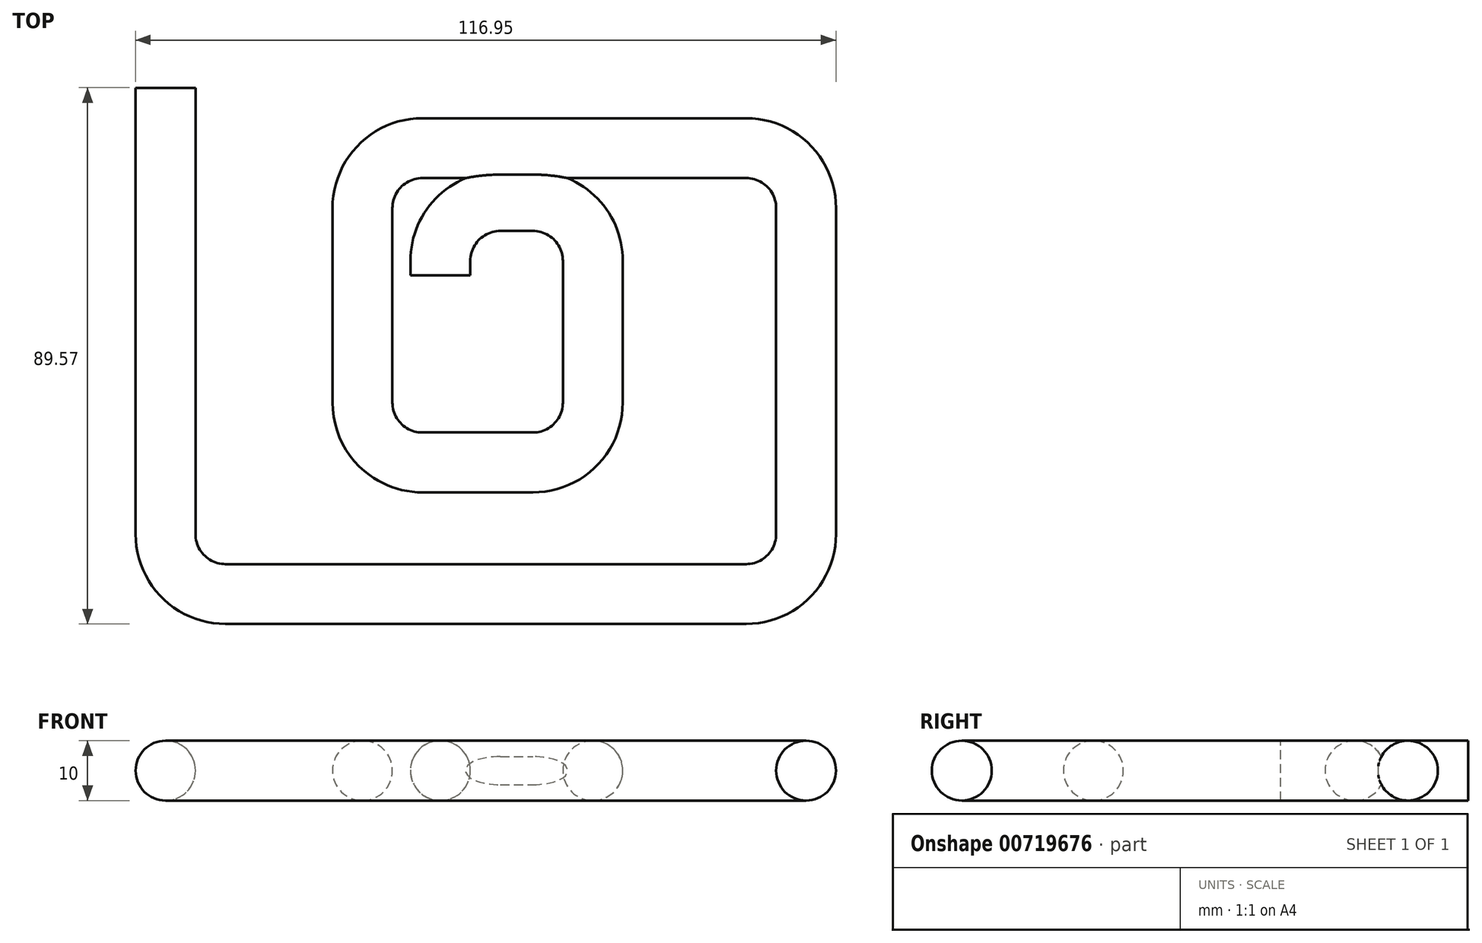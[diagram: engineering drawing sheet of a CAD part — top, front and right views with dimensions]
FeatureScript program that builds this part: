
annotation { "Feature Type Name" : "Feature", "Feature Type Description" : "" }
export const myFeature = defineFeature(function(context is Context, id is Id, definition is map)
    precondition{}
    {
        {
            var Q0;
            Q0=qCreatedBy(makeId("Front.planeOp"),FACE);
            var sketch = newSketch(context, id + "F0", { "sketchPlane" : qUnion([Q0])});
            skCircle(sketch, "E0", {"center": v(0, 0) * mm, "radius": 5 * mm});
            skSolve(sketch);
        }
        {
            var Q0;
            Q0=qCreatedBy(makeId("Top.planeOp"),FACE);
            var sketch = newSketch(context, id + "F1", { "sketchPlane" : qUnion([Q0])});
            skLineSegment(sketch, "E1", {"start": v(-45.89, 31.34) * mm, "end": v(-45.89, -43.23) * mm});
            skLineSegment(sketch, "E2", {"start": v(-35.89, -53.23) * mm, "end": v(51.06, -53.23) * mm});
            skLineSegment(sketch, "E3", {"start": v(61.06, -43.23) * mm, "end": v(61.06, 11.25) * mm});
            skLineSegment(sketch, "E4", {"start": v(51.06, 21.25) * mm, "end": v(-3, 21.25) * mm});
            skLineSegment(sketch, "E5", {"start": v(-13, 11.25) * mm, "end": v(-13, -21.25) * mm});
            skLineSegment(sketch, "E6", {"start": v(-3, -31.25) * mm, "end": v(15.45, -31.25) * mm});
            skLineSegment(sketch, "E7", {"start": v(25.45, -21.25) * mm, "end": v(25.45, -10.9) * mm});
            skPoint(sketch, "E8.visualSharp", {"position": v(-45.89, -53.23) * mm});
            skArc(sketch, "E8.filletArc", {"start": v(-45.89, -43.23) * mm, "mid": v(-42.96, -50.3) * mm, "end": v(-35.89, -53.23) * mm});
            skPoint(sketch, "E9.visualSharp", {"position": v(61.06, -53.23) * mm});
            skArc(sketch, "E9.filletArc", {"start": v(51.06, -53.23) * mm, "mid": v(58.13, -50.3) * mm, "end": v(61.06, -43.23) * mm});
            skPoint(sketch, "E10.visualSharp", {"position": v(61.06, 21.25) * mm});
            skArc(sketch, "E10.filletArc", {"start": v(61.06, 11.25) * mm, "mid": v(58.13, 18.32) * mm, "end": v(51.06, 21.25) * mm});
            skPoint(sketch, "E11.visualSharp", {"position": v(-13, 21.25) * mm});
            skArc(sketch, "E11.filletArc", {"start": v(-3, 21.25) * mm, "mid": v(-10.08, 18.32) * mm, "end": v(-13, 11.25) * mm});
            skPoint(sketch, "E12.visualSharp", {"position": v(25.45, -31.25) * mm});
            skArc(sketch, "E12.filletArc", {"start": v(15.45, -31.25) * mm, "mid": v(22.52, -28.32) * mm, "end": v(25.45, -21.25) * mm});
            skPoint(sketch, "E13.visualSharp", {"position": v(-13, -31.25) * mm});
            skArc(sketch, "E13.filletArc", {"start": v(-13, -21.25) * mm, "mid": v(-10.08, -28.32) * mm, "end": v(-3, -31.25) * mm});
            skLineSegment(sketch, "E14", {"start": v(25.45, -10.9) * mm, "end": v(25.45, -4.91) * mm});
            skLineSegment(sketch, "E15", {"start": v(25.45, -4.91) * mm, "end": v(25.45, 2.41) * mm});
            skLineSegment(sketch, "E16", {"start": v(15.45, 12.41) * mm, "end": v(10, 12.41) * mm});
            skLineSegment(sketch, "E17", {"start": v(0, 2.41) * mm, "end": v(0, 0) * mm});
            skPoint(sketch, "E18.visualSharp", {"position": v(25.45, 12.41) * mm});
            skArc(sketch, "E18.filletArc", {"start": v(25.45, 2.41) * mm, "mid": v(22.52, 9.48) * mm, "end": v(15.45, 12.41) * mm});
            skPoint(sketch, "E19.visualSharp", {"position": v(0, 12.41) * mm});
            skArc(sketch, "E19.filletArc", {"start": v(10, 12.41) * mm, "mid": v(2.93, 9.48) * mm, "end": v(0, 2.41) * mm});
            skSolve(sketch);
        }
        {
            var Q0;
            Q0=makeQuery(id+"F0.imprint","IMPRINT",FACE,{"disambiguationData":[TD([[makeQuery(id+"F0.imprint","IMPRINT",EDGE,{"derivedFrom":sQuery(id+"F0.wireOp",EDGE,"E0")}),1.0]])]});
            var Q1;
            Q1 = qConstructionFilter(qBodyType(qCreatedBy(id + "F1" ,EDGE), BodyType.WIRE), ConstructionObject.NO);
            sweep(context, id + "F2", {"profiles" : qUnion([Q0]), "path" : qUnion([Q1])});
        }
    });
